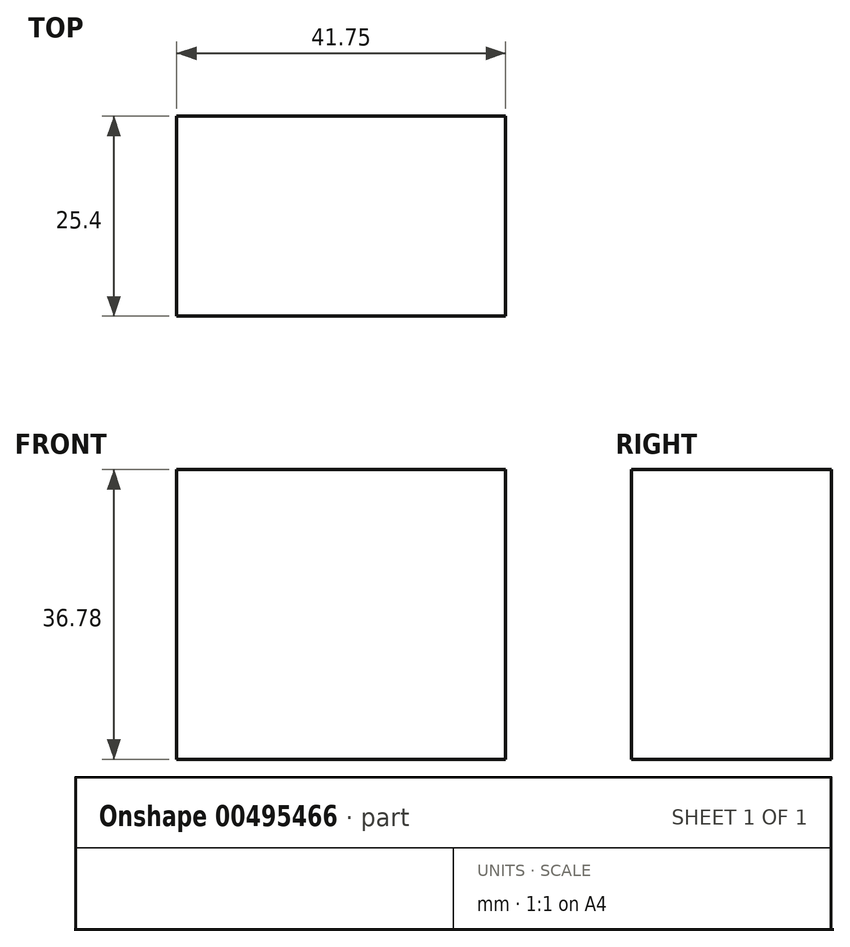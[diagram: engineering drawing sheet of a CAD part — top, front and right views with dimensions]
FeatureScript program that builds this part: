
annotation { "Feature Type Name" : "Feature", "Feature Type Description" : "" }
export const myFeature = defineFeature(function(context is Context, id is Id, definition is map)
    precondition{}
    {
        {
            var Q0;
            Q0=qCreatedBy(makeId("Front.planeOp"),FACE);
            var sketch = newSketch(context, id + "F0", { "sketchPlane" : qUnion([Q0])});
            skLineSegment(sketch, "E0.bottom", {"start": v(-48.57, 36.78) * mm, "end": v(-6.82, 36.78) * mm});
            skLineSegment(sketch, "E0.top", {"start": v(-48.57, 0) * mm, "end": v(-6.82, 0) * mm});
            skLineSegment(sketch, "E0.left", {"start": v(-48.57, 36.78) * mm, "end": v(-48.57, 0) * mm});
            skLineSegment(sketch, "E0.right", {"start": v(-6.82, 36.78) * mm, "end": v(-6.82, 0) * mm});
            skSolve(sketch);
        }
        {
            var Q0;
            Q0=makeQuery(id+"F0.imprint","IMPRINT",FACE,{"disambiguationData":[TD([[makeQuery(id+"F0.imprint","IMPRINT",EDGE,{"derivedFrom":sQuery(id+"F0.wireOp",EDGE,"E0.bottom")}),-1.0]])]});
            extrude(context, id + "F1", {"entities" : qUnion([Q0]), "depth" : 25.4 * mm});
        }
    });
